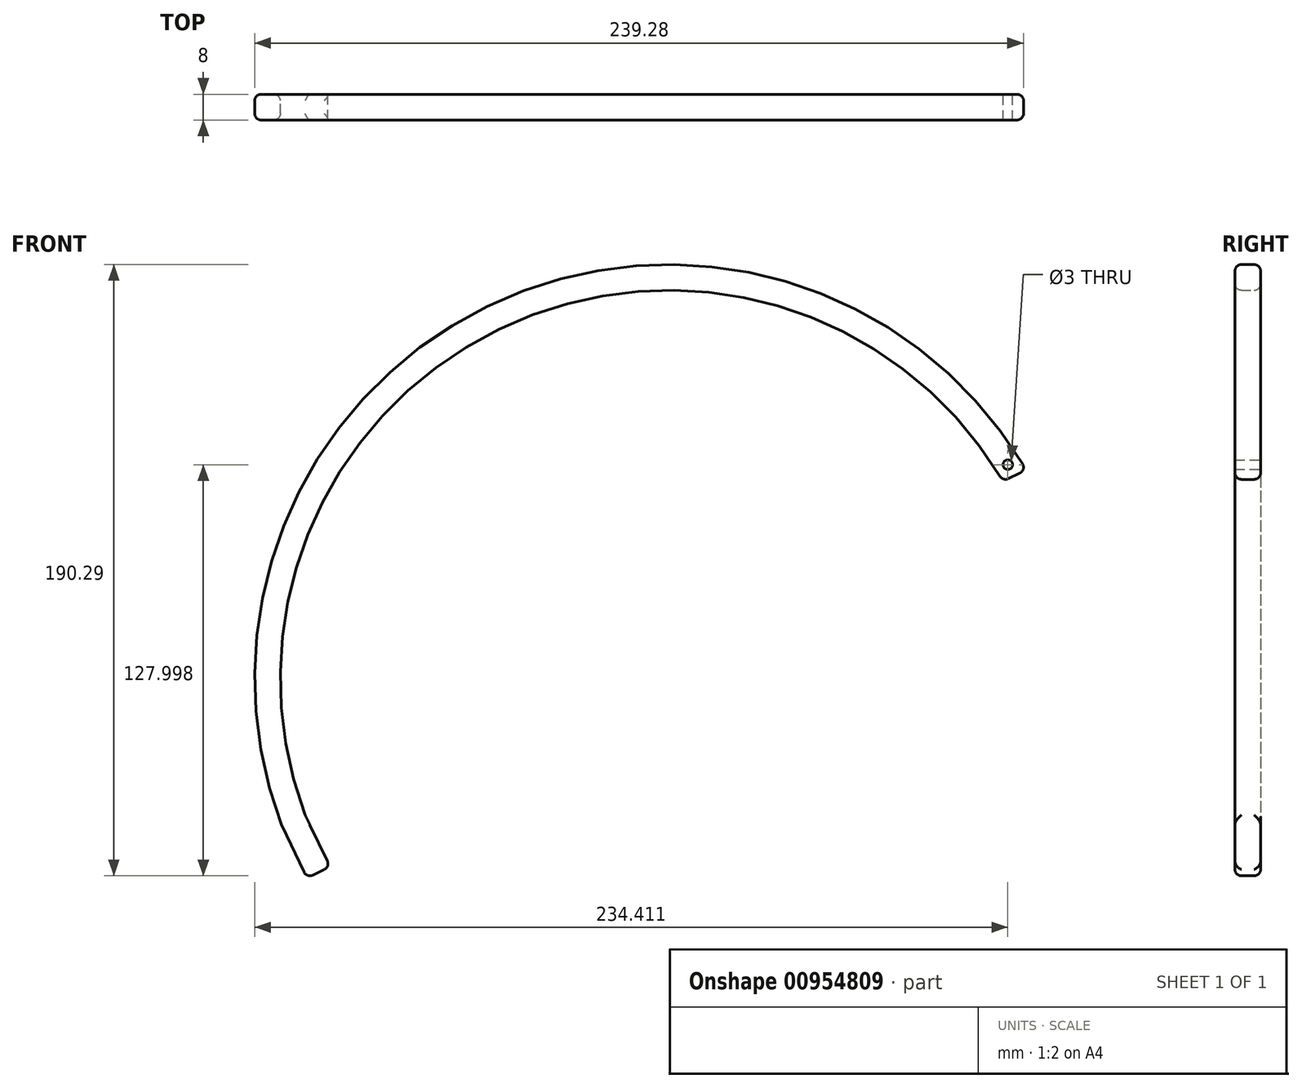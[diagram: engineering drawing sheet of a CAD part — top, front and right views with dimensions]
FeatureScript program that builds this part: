
annotation { "Feature Type Name" : "Feature", "Feature Type Description" : "" }
export const myFeature = defineFeature(function(context is Context, id is Id, definition is map)
    precondition{}
    {
        {
            var Q0;
            Q0=qCreatedBy(makeId("Front.planeOp"),FACE);
            var sketch = newSketch(context, id + "F0", { "sketchPlane" : qUnion([Q0])});
            skLineSegment(sketch, "E0.bottom", {"start": v(120, 100) * mm, "end": v(-120, 100) * mm, "construction": true});
            skLineSegment(sketch, "E0.top", {"start": v(120, -100) * mm, "end": v(-120, -100) * mm, "construction": true});
            skLineSegment(sketch, "E0.left", {"start": v(120, 100) * mm, "end": v(120, -100) * mm, "construction": true});
            skLineSegment(sketch, "E0.right", {"start": v(-120, 100) * mm, "end": v(-120, -100) * mm, "construction": true});
            skPoint(sketch, "E0.middle", {"position": v(0, 0) * mm});
            skArc(sketch, "E1", {"start": v(120, 28.51) * mm, "mid": v(-46.86, 79.92) * mm, "end": v(-111.66, -82.2) * mm});
            skLineSegment(sketch, "E2", {"start": v(-111.66, -82.2) * mm, "end": v(138.1, 37.16) * mm, "construction": true});
            skLineSegment(sketch, "E3", {"start": v(13.22, -22.52) * mm, "end": v(-46.86, 79.92) * mm, "construction": true});
            skArc(sketch, "E4.0", {"start": v(112.76, 25.05) * mm, "mid": v(-43.4, 72.7) * mm, "end": v(-104.41, -78.75) * mm});
            skLineSegment(sketch, "E5", {"start": v(-111.66, -82.2) * mm, "end": v(-104.41, -78.75) * mm});
            skLineSegment(sketch, "E6", {"start": v(112.76, 25.05) * mm, "end": v(120, 28.51) * mm});
            skCircle(sketch, "E7", {"center": v(114.3, 30.22) * mm, "radius": 1.5 * mm});
            skLineSegment(sketch, "E8", {"start": v(-111.66, -82.2) * mm, "end": v(-103.9, -98.45) * mm});
            skLineSegment(sketch, "E9", {"start": v(-103.9, -98.45) * mm, "end": v(-96.65, -94.99) * mm});
            skLineSegment(sketch, "E10", {"start": v(-96.65, -94.99) * mm, "end": v(-104.41, -78.75) * mm});
            skSolve(sketch);
        }
        {
            var Q0;
            Q0 = qSketchRegion(id + "F0", true);
            extrude(context, id + "F1", {"entities" : qUnion([Q0]), "depth" : 8 * mm, "offsetDistance" : 25 * mm});
        }
        {
            var Q0;
            Q0=makeQuery(id+"F1.opExtrude","CAP_EDGE",EDGE,{"disambiguationData":[OSD([sQuery(id+"F0.wireOp",EDGE,"E4.0")])],"isStart":false});
            var Q1;
            Q1=makeQuery(id+"F1.opExtrude","CAP_EDGE",EDGE,{"disambiguationData":[OSD([sQuery(id+"F0.wireOp",EDGE,"E1")])],"isStart":false});
            var Q2;
            Q2=makeQuery(id+"F1.opExtrude","CAP_EDGE",EDGE,{"disambiguationData":[OSD([sQuery(id+"F0.wireOp",EDGE,"E5")])],"isStart":false});
            var Q3;
            Q3=makeQuery(id+"F1.opExtrude","SWEPT_EDGE",EDGE,{"disambiguationData":[OSD([sQuery(id+"F0.wireOp",EDGE,"E1"),sQuery(id+"F0.wireOp",EDGE,"E5")])]});
            var Q4;
            Q4=makeQuery(id+"F1.opExtrude","SWEPT_EDGE",EDGE,{"disambiguationData":[OSD([sQuery(id+"F0.wireOp",EDGE,"E4.0"),sQuery(id+"F0.wireOp",EDGE,"E5")])]});
            var Q5;
            Q5=makeQuery(id+"F1.opExtrude","CAP_EDGE",EDGE,{"disambiguationData":[OSD([sQuery(id+"F0.wireOp",EDGE,"E4.0")])],"isStart":true});
            var Q6;
            Q6=makeQuery(id+"F1.opExtrude","CAP_EDGE",EDGE,{"disambiguationData":[OSD([sQuery(id+"F0.wireOp",EDGE,"E1")])],"isStart":true});
            var Q7;
            Q7=makeQuery(id+"F1.opExtrude","SWEPT_EDGE",EDGE,{"disambiguationData":[OSD([sQuery(id+"F0.wireOp",EDGE,"E1"),sQuery(id+"F0.wireOp",EDGE,"E6")])]});
            var Q8;
            Q8=makeQuery(id+"F1.opExtrude","CAP_EDGE",EDGE,{"disambiguationData":[OSD([sQuery(id+"F0.wireOp",EDGE,"E6")])],"isStart":false});
            var Q9;
            Q9=makeQuery(id+"F1.opExtrude","SWEPT_EDGE",EDGE,{"disambiguationData":[OSD([sQuery(id+"F0.wireOp",EDGE,"E4.0"),sQuery(id+"F0.wireOp",EDGE,"E6")])]});
            var Q10;
            Q10=makeQuery(id+"F1.opExtrude","CAP_EDGE",EDGE,{"disambiguationData":[OSD([sQuery(id+"F0.wireOp",EDGE,"E6")])],"isStart":true});
            var Q11;
            Q11=makeQuery(id+"F1.opExtrude","CAP_EDGE",EDGE,{"disambiguationData":[OSD([sQuery(id+"F0.wireOp",EDGE,"E5")])],"isStart":true});
            var Q12;
            Q12=makeQuery(id+"F1.opExtrude","CAP_EDGE",EDGE,{"disambiguationData":[OSD([sQuery(id+"F0.wireOp",EDGE,"E8")])],"isStart":false});
            var Q13;
            Q13=makeQuery(id+"F1.opExtrude","CAP_EDGE",EDGE,{"disambiguationData":[OSD([sQuery(id+"F0.wireOp",EDGE,"E8")])],"isStart":true});
            var Q14;
            Q14=makeQuery(id+"F1.opExtrude","CAP_EDGE",EDGE,{"disambiguationData":[OSD([sQuery(id+"F0.wireOp",EDGE,"E9")])],"isStart":false});
            var Q15;
            Q15=makeQuery(id+"F1.opExtrude","SWEPT_EDGE",EDGE,{"disambiguationData":[OSD([sQuery(id+"F0.wireOp",EDGE,"E8"),sQuery(id+"F0.wireOp",EDGE,"E9")])]});
            var Q16;
            Q16=makeQuery(id+"F1.opExtrude","SWEPT_EDGE",EDGE,{"disambiguationData":[OSD([sQuery(id+"F0.wireOp",EDGE,"E9"),sQuery(id+"F0.wireOp",EDGE,"E10")])]});
            var Q17;
            Q17=makeQuery(id+"F1.opExtrude","CAP_EDGE",EDGE,{"disambiguationData":[OSD([sQuery(id+"F0.wireOp",EDGE,"E9")])],"isStart":true});
            fillet(context, id + "F2", {"entities" : qUnion([Q0, Q1, Q2, Q3, Q4, Q5, Q6, Q7, Q8, Q9, Q10, Q11, Q12, Q13, Q14, Q15, Q16, Q17]), "radius" : 2 * mm, "tangentPropagation" : true, "allowEdgeOverflow" : false});
        }
    });
